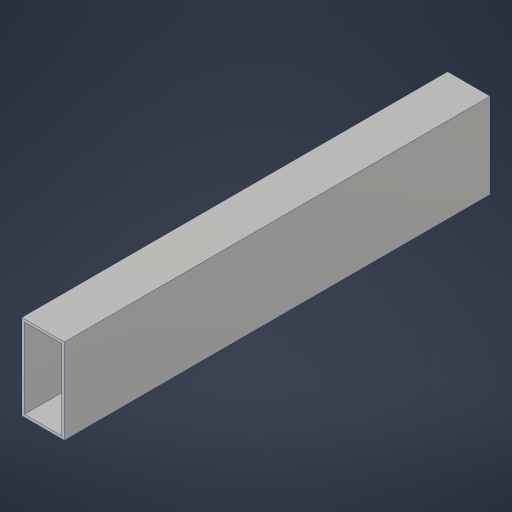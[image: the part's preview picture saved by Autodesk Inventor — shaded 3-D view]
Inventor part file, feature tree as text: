
AUTODESK INVENTOR PART (.ipt)
format: ipt  version: 2023.4 (Build 274418000, 418)  size: 171,520 bytes
history: native  units: in
note: dims shown in document units (in); Inventor stores cm internally (conversion verified against a paired STEP export)
features: extrude x1
ambient origin geometry x8: Origin, YZ Plane, XZ Plane, XY Plane, X Axis, Y Axis, Z Axis, Center Point
bodies: Solid1 (feature_tree)
feature tree (1):
  extrude  "Extrusion1"  TaperAngle=0.0deg  [1 undecoded]
note: 1 required parameter value undecoded (feature->parameter linkage not recoverable at this tier; creation-order binding heuristic only, values carry confidence <= 0.55)
